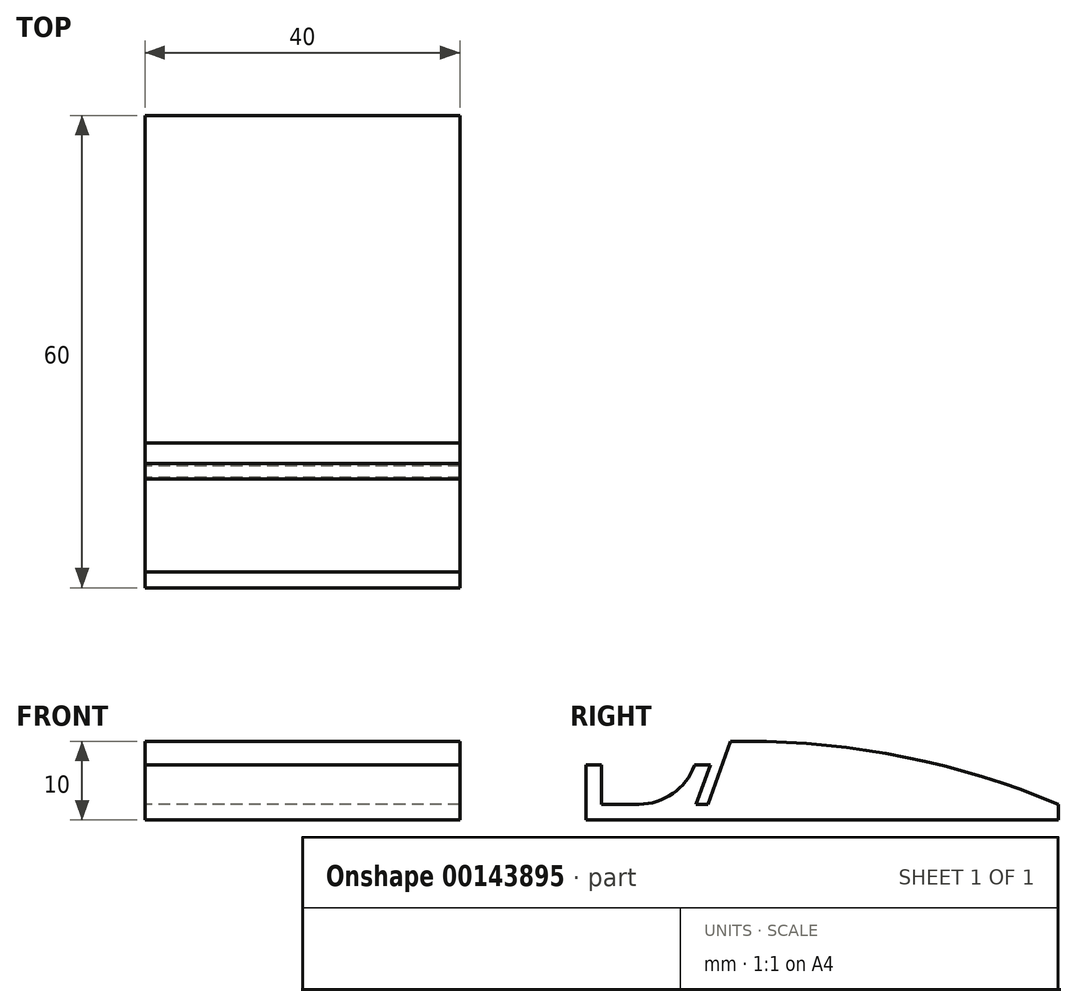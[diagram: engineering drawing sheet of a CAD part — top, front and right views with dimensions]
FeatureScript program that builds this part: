
annotation { "Feature Type Name" : "Feature", "Feature Type Description" : "" }
export const myFeature = defineFeature(function(context is Context, id is Id, definition is map)
    precondition{}
    {
        {
            var Q0;
            Q0=qCreatedBy(makeId("Right.planeOp"),FACE);
            var sketch = newSketch(context, id + "F0", { "sketchPlane" : qUnion([Q0])});
            skLineSegment(sketch, "E0", {"start": v(0, 0) * mm, "end": v(0, -2) * mm});
            skLineSegment(sketch, "E1", {"start": v(0, -2) * mm, "end": v(-60, -2) * mm});
            skLineSegment(sketch, "E2", {"start": v(-60, -2) * mm, "end": v(-60, 5) * mm});
            skLineSegment(sketch, "E3", {"start": v(-60, 5) * mm, "end": v(-58, 5) * mm});
            skLineSegment(sketch, "E4", {"start": v(-58, 5) * mm, "end": v(-58, 0) * mm});
            skLineSegment(sketch, "E5", {"start": v(-58, 0) * mm, "end": v(-48, 0) * mm});
            skLineSegment(sketch, "E6", {"start": v(-48, 0) * mm, "end": v(-46.18, 5) * mm});
            skLineSegment(sketch, "E7", {"start": v(-46.18, 5) * mm, "end": v(-44.18, 5) * mm});
            skLineSegment(sketch, "E8", {"start": v(-44.18, 5) * mm, "end": v(-46, 0) * mm});
            skLineSegment(sketch, "E9", {"start": v(-46, 0) * mm, "end": v(-44.51, 0) * mm});
            skLineSegment(sketch, "E10", {"start": v(-44.51, 0) * mm, "end": v(-41.6, 8) * mm});
            skLineSegment(sketch, "E11", {"start": v(-41.6, 8) * mm, "end": v(-39.6, 8) * mm});
            skArc(sketch, "E12", {"start": v(0, 0) * mm, "mid": v(-19.4, 5.98) * mm, "end": v(-39.6, 8) * mm});
            skSolve(sketch);
        }
        {
            var Q0;
            Q0=makeQuery(id+"F0.imprint","IMPRINT",FACE,{"disambiguationData":[TD([[makeQuery(id+"F0.imprint","IMPRINT",EDGE,{"derivedFrom":sQuery(id+"F0.wireOp",EDGE,"E0")}),-1.0]])]});
            extrude(context, id + "F1", {"entities" : qUnion([Q0]), "depth" : 40 * mm});
        }
        {
            var Q0;
            Q0=makeQuery(id+"F1.opExtrude","SWEPT_EDGE",EDGE,{"disambiguationData":[OSD([sQuery(id+"F0.wireOp",EDGE,"E5"),sQuery(id+"F0.wireOp",EDGE,"E6")])]});
            fillet(context, id + "F2", {"entities" : qUnion([Q0]), "radius" : 7.5 * mm, "tangentPropagation" : true, "allowEdgeOverflow" : false});
        }
    });
